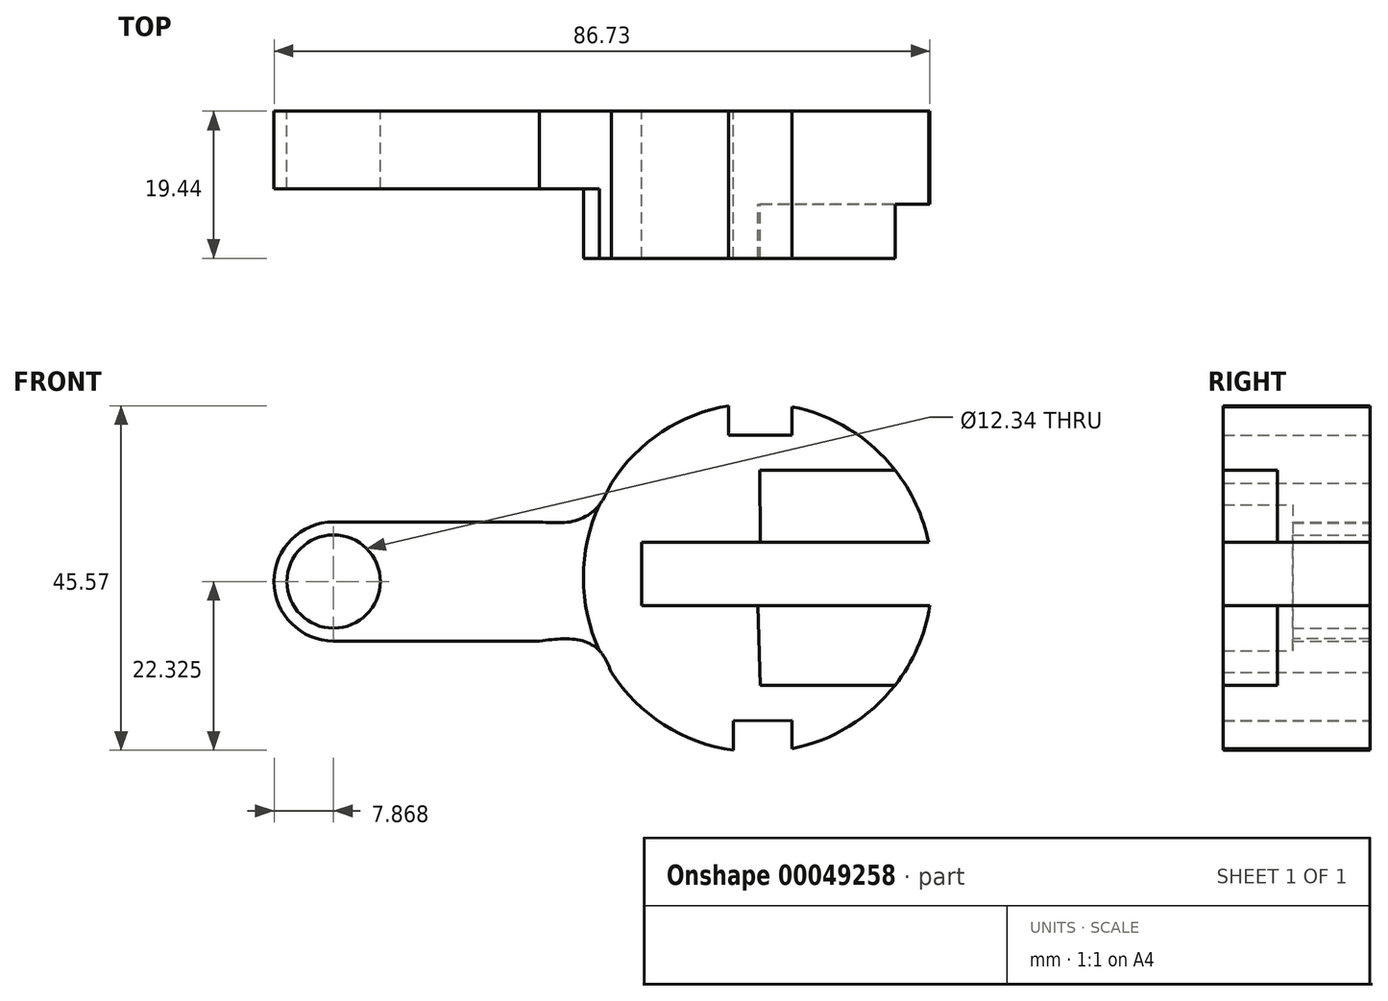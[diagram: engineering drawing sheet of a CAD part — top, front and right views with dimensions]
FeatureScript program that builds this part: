
annotation { "Feature Type Name" : "Feature", "Feature Type Description" : "" }
export const myFeature = defineFeature(function(context is Context, id is Id, definition is map)
    precondition{}
    {
        {
            var Q0;
            Q0=qCreatedBy(makeId("Front.planeOp"),FACE);
            var sketch = newSketch(context, id + "F0", { "sketchPlane" : qUnion([Q0])});
            skArc(sketch, "E0", {"start": v(51.44, 4.67) * mm, "mid": v(5.8, -0.49) * mm, "end": v(51.62, -3.71) * mm});
            skLineSegment(sketch, "E1", {"start": v(51.44, 4.67) * mm, "end": v(13.52, 4.67) * mm});
            skLineSegment(sketch, "E2", {"start": v(51.62, -3.71) * mm, "end": v(13.52, -3.71) * mm});
            skLineSegment(sketch, "E3", {"start": v(13.52, -3.71) * mm, "end": v(13.52, 4.67) * mm});
            skLineSegment(sketch, "E4", {"start": v(51.44, 4.67) * mm, "end": v(60.74, 4.67) * mm});
            skLineSegment(sketch, "E5", {"start": v(51.62, -3.71) * mm, "end": v(60.74, -3.71) * mm});
            skLineSegment(sketch, "E6", {"start": v(60.74, -3.71) * mm, "end": v(60.74, 4.67) * mm});
            skFitSpline(sketch, "E7", {"points": [v(9.5, 12.53) * mm, v(7.9, 9.65) * mm, v(4.84, 7.57) * mm, v(0, 7.37) * mm], "startDerivative": vector(-4.7, -9.62) * mm, "endDerivative": vector(-13.8, 0.92) * mm});
            skLineSegment(sketch, "E8", {"start": v(0, 7.37) * mm, "end": v(-27.24, 7.37) * mm});
            skFitSpline(sketch, "E9", {"points": [v(9.5, -12.53) * mm, v(7.9, -9.65) * mm, v(4.84, -8.17) * mm, v(0, -8.37) * mm], "startDerivative": vector(-4.03, 10.26) * mm, "endDerivative": vector(-13.42, -1.64) * mm});
            skLineSegment(sketch, "E10", {"start": v(0, -8.37) * mm, "end": v(-27.24, -8.37) * mm});
            skArc(sketch, "E11", {"start": v(-27.24, 7.37) * mm, "mid": v(-35.11, -0.5) * mm, "end": v(-27.24, -8.37) * mm});
            skCircle(sketch, "E12", {"center": v(-27.24, -0.5) * mm, "radius": 3.34 * mm});
            skLineSegment(sketch, "E13", {"start": v(-35.11, -0.5) * mm, "end": v(57.3, 0) * mm, "construction": true});
            skLineSegment(sketch, "E14", {"start": v(33.38, 23.06) * mm, "end": v(33.38, 18.87) * mm});
            skLineSegment(sketch, "E15", {"start": v(33.38, 18.87) * mm, "end": v(25.02, 18.87) * mm});
            skLineSegment(sketch, "E16", {"start": v(25.02, 18.87) * mm, "end": v(25.02, 22.74) * mm});
            skLineSegment(sketch, "E17", {"start": v(33.38, -22.61) * mm, "end": v(33.36, -18.87) * mm});
            skLineSegment(sketch, "E18", {"start": v(33.36, -18.87) * mm, "end": v(25.63, -18.91) * mm});
            skLineSegment(sketch, "E19", {"start": v(25.63, -18.91) * mm, "end": v(25.63, -22.83) * mm});
            skLineSegment(sketch, "E20", {"start": v(29.2, 4.67) * mm, "end": v(29.15, 14.23) * mm});
            skPoint(sketch, "E20.startSnap0", {"position": v(29.2, 18.87) * mm});
            skLineSegment(sketch, "E21", {"start": v(29.15, 14.23) * mm, "end": v(47, 14.23) * mm});
            skLineSegment(sketch, "E22", {"start": v(28.86, -3.71) * mm, "end": v(29.2, -14.23) * mm});
            skLineSegment(sketch, "E23", {"start": v(29.2, -14.23) * mm, "end": v(47, -14.23) * mm});
            skCircle(sketch, "E24", {"center": v(-27.24, -0.5) * mm, "radius": 6.17 * mm});
            skSolve(sketch);
        }
        {
            var Q0;
            {var subQ6=sQuery(id+"F0.wireOp",EDGE,"E8");Q0=makeQuery(id+"F0.imprint","IMPRINT",FACE,{"disambiguationData":[TD([[makeQuery(id+"F0.imprint","IMPRINT",EDGE,{"derivedFrom":subQ6}),1.0]])]});}
            extrude(context, id + "F1", {"entities" : qUnion([Q0]), "depth" : 10.25 * mm});
        }
        {
            var Q0;
            {var subQ14=sQuery(id+"F0.wireOp",EDGE,"E3");Q0=makeQuery(id+"F0.imprint","IMPRINT",FACE,{"disambiguationData":[TD([[makeQuery(id+"F0.imprint","IMPRINT",EDGE,{"derivedFrom":subQ14}),1.0]])]});}
            extrude(context, id + "F2", {"entities" : qUnion([Q0]), "operationType" : NewBodyOperationType.ADD, "depth" : 19.44 * mm});
        }
        {
            var Q0;
            {var subQ1=sQuery(id+"F0.wireOp",EDGE,"E22");Q0=makeQuery(id+"F0.imprint","IMPRINT",FACE,{"disambiguationData":[TD([[makeQuery(id+"F0.imprint","IMPRINT",EDGE,{"derivedFrom":subQ1}),1.0]])]});}
            var Q1;
            {var subQ1=sQuery(id+"F0.wireOp",EDGE,"E20");Q1=makeQuery(id+"F0.imprint","IMPRINT",FACE,{"disambiguationData":[TD([[makeQuery(id+"F0.imprint","IMPRINT",EDGE,{"derivedFrom":subQ1}),-1.0]])]});}
            extrude(context, id + "F3", {"entities" : qUnion([Q0, Q1]), "operationType" : NewBodyOperationType.ADD, "depth" : 12.3 * mm});
        }
        {
            var Q0;
            Q0=sQuery(id+"F0.wireOp",EDGE,"E24");
            extrude(context, id + "F4", {"bodyType" : ToolBodyType.SURFACE, "surfaceEntities" : qUnion([Q0]), "depth" : 9.43 * mm});
        }
    });
